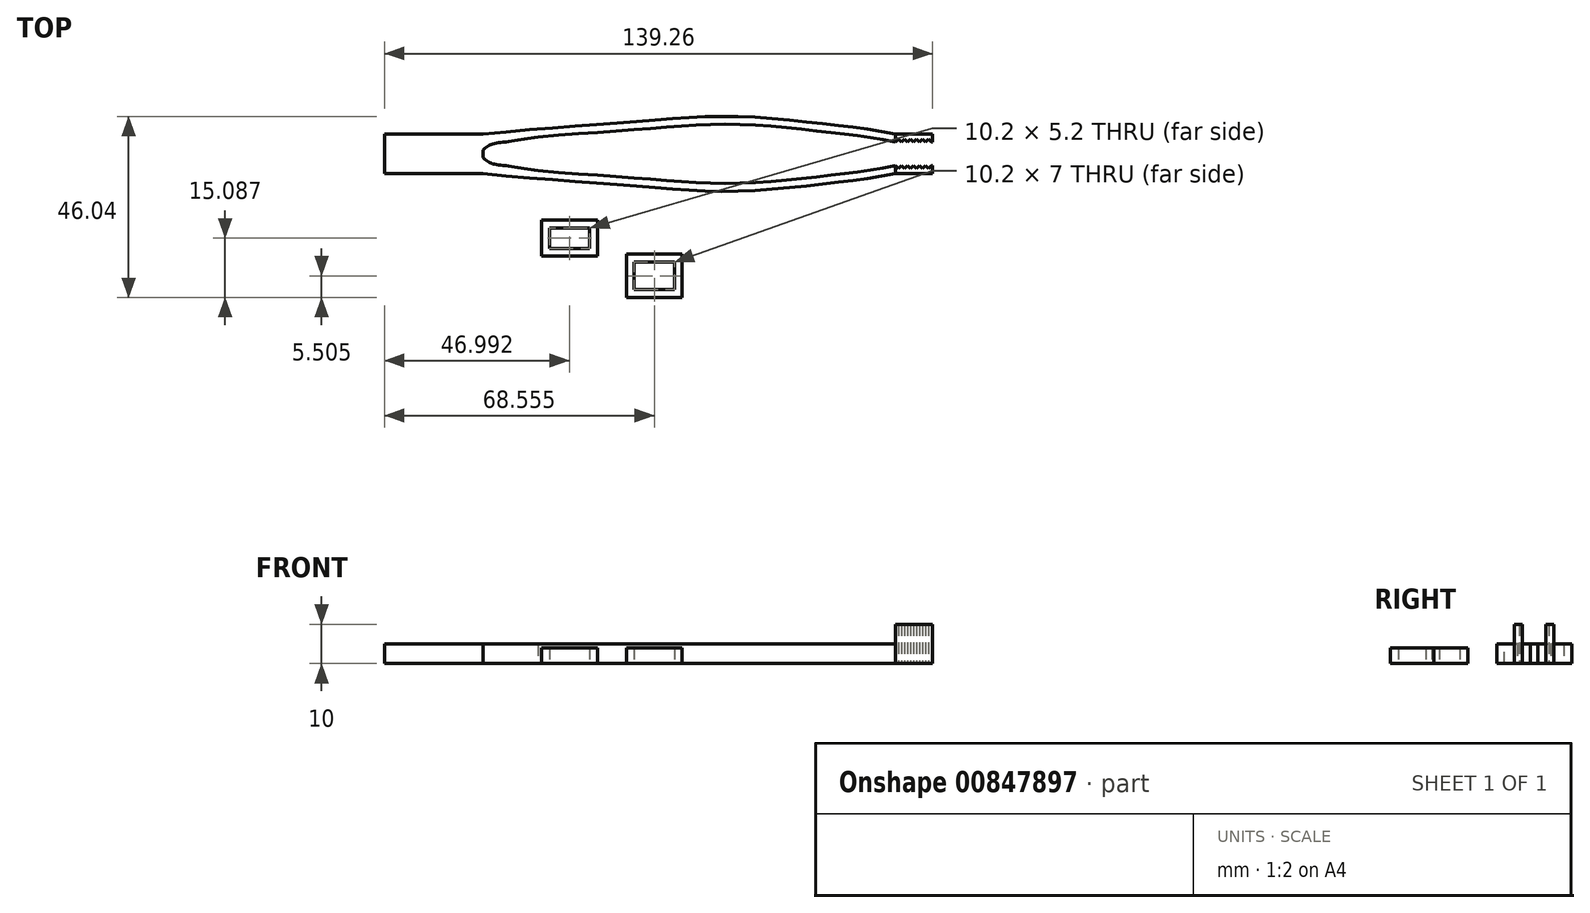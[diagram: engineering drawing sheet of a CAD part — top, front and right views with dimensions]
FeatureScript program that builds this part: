
annotation { "Feature Type Name" : "Feature", "Feature Type Description" : "" }
export const myFeature = defineFeature(function(context is Context, id is Id, definition is map)
    precondition{}
    {
        {
            var Q0;
            Q0=qCreatedBy(makeId("Top.planeOp"),FACE);
            var sketch = newSketch(context, id + "F0", { "sketchPlane" : qUnion([Q0])});
            skLineSegment(sketch, "E0.bottom", {"start": v(-68.5, 5) * mm, "end": v(-93.5, 5) * mm});
            skLineSegment(sketch, "E0.top", {"start": v(-68.5, -5) * mm, "end": v(-93.5, -5) * mm});
            skLineSegment(sketch, "E0.left", {"start": v(-68.5, 0.93) * mm, "end": v(-68.5, -0.93) * mm});
            skLineSegment(sketch, "E0.right", {"start": v(-93.5, 5) * mm, "end": v(-93.5, -5) * mm});
            skPoint(sketch, "E0.middle", {"position": v(-81, 0) * mm});
            skFitSpline(sketch, "E1", {"points": [v(-68.5, 5) * mm, v(-28.51, 8.25) * mm, v(-5, 9.51) * mm, v(18.78, 7.55) * mm, v(36.26, 5) * mm], "startDerivative": vector(137.3, 14.39) * mm, "endDerivative": vector(80, -17.34) * mm});
            skFitSpline(sketch, "E2", {"points": [v(-68.5, 3) * mm, v(-28.51, 6.25) * mm, v(-5, 7.51) * mm, v(18.78, 5.55) * mm, v(36.26, 3) * mm], "startDerivative": vector(137.3, 14.39) * mm, "endDerivative": vector(80, -17.34) * mm});
            skLineSegment(sketch, "E3.bottom", {"start": v(45.46, 3) * mm, "end": v(45.76, 3) * mm});
            skLineSegment(sketch, "E3.top", {"start": v(36.26, 5) * mm, "end": v(45.76, 5) * mm});
            skLineSegment(sketch, "E3.right", {"start": v(45.76, 3) * mm, "end": v(45.76, 5) * mm});
            skFitSpline(sketch, "E4.MirrorCS", {"points": [v(-68.5, -5) * mm, v(-28.51, -8.25) * mm, v(-5, -9.51) * mm, v(18.78, -7.55) * mm, v(36.26, -5) * mm], "startDerivative": vector(137.3, -14.39) * mm, "endDerivative": vector(80, 17.34) * mm});
            skFitSpline(sketch, "E5.MirrorCS", {"points": [v(-68.5, -3) * mm, v(-28.51, -6.25) * mm, v(-5, -7.51) * mm, v(18.78, -5.55) * mm, v(36.26, -3) * mm], "startDerivative": vector(137.3, -14.39) * mm, "endDerivative": vector(80, 17.34) * mm});
            skLineSegment(sketch, "E6.MirrorCS", {"start": v(36.26, -5) * mm, "end": v(45.76, -5) * mm});
            skLineSegment(sketch, "E7.MirrorCS", {"start": v(45.46, -3) * mm, "end": v(45.76, -3) * mm});
            skLineSegment(sketch, "E8.MirrorCS", {"start": v(45.76, -3) * mm, "end": v(45.76, -5) * mm});
            skLineSegment(sketch, "E9", {"start": v(36.26, 3) * mm, "end": v(37.06, 3.77) * mm});
            skLineSegment(sketch, "E10", {"start": v(37.06, 3.77) * mm, "end": v(37.8, 3) * mm});
            skPoint(sketch, "E11.middle", {"position": v(-34.21, 3.16) * mm});
            skLineSegment(sketch, "E12", {"start": v(37.8, 3) * mm, "end": v(38.59, 3.77) * mm});
            skLineSegment(sketch, "E13", {"start": v(38.59, 3.77) * mm, "end": v(39.33, 3) * mm});
            skLineSegment(sketch, "E14", {"start": v(39.33, 3) * mm, "end": v(40.12, 3.77) * mm});
            skLineSegment(sketch, "E15", {"start": v(40.12, 3.77) * mm, "end": v(40.86, 3) * mm});
            skLineSegment(sketch, "E16", {"start": v(40.86, 3) * mm, "end": v(41.65, 3.77) * mm});
            skLineSegment(sketch, "E17", {"start": v(41.65, 3.77) * mm, "end": v(42.4, 3) * mm});
            skLineSegment(sketch, "E18", {"start": v(42.4, 3) * mm, "end": v(43.19, 3.77) * mm});
            skLineSegment(sketch, "E19", {"start": v(43.19, 3.77) * mm, "end": v(43.93, 3) * mm});
            skLineSegment(sketch, "E20", {"start": v(43.93, 3) * mm, "end": v(44.72, 3.77) * mm});
            skLineSegment(sketch, "E21", {"start": v(44.72, 3.77) * mm, "end": v(45.46, 3) * mm});
            skLineSegment(sketch, "E22.MirrorCS", {"start": v(36.26, -3) * mm, "end": v(37.06, -3.77) * mm});
            skLineSegment(sketch, "E23.MirrorCS", {"start": v(37.06, -3.77) * mm, "end": v(37.8, -3) * mm});
            skLineSegment(sketch, "E24.MirrorCS", {"start": v(37.8, -3) * mm, "end": v(38.59, -3.77) * mm});
            skLineSegment(sketch, "E25.MirrorCS", {"start": v(38.59, -3.77) * mm, "end": v(39.33, -3) * mm});
            skLineSegment(sketch, "E26.MirrorCS", {"start": v(39.33, -3) * mm, "end": v(40.12, -3.77) * mm});
            skLineSegment(sketch, "E27.MirrorCS", {"start": v(40.12, -3.77) * mm, "end": v(40.86, -3) * mm});
            skLineSegment(sketch, "E28.MirrorCS", {"start": v(40.86, -3) * mm, "end": v(41.65, -3.77) * mm});
            skLineSegment(sketch, "E29.MirrorCS", {"start": v(41.65, -3.77) * mm, "end": v(42.4, -3) * mm});
            skLineSegment(sketch, "E30.MirrorCS", {"start": v(42.4, -3) * mm, "end": v(43.19, -3.77) * mm});
            skLineSegment(sketch, "E31.MirrorCS", {"start": v(43.19, -3.77) * mm, "end": v(43.93, -3) * mm});
            skLineSegment(sketch, "E32.MirrorCS", {"start": v(43.93, -3) * mm, "end": v(44.72, -3.77) * mm});
            skLineSegment(sketch, "E33.MirrorCS", {"start": v(44.72, -3.77) * mm, "end": v(45.46, -3) * mm});
            skPoint(sketch, "E34.orphan", {"position": v(-46.71, -1.84) * mm});
            skPoint(sketch, "E11.right.start.orphan", {"position": v(-46.71, 8.16) * mm});
            skPoint(sketch, "E35.orphan", {"position": v(-21.71, -1.84) * mm});
            skPoint(sketch, "E11.bottom.start.orphan", {"position": v(-21.71, 8.16) * mm});
            skFitSpline(sketch, "E36", {"points": [v(-68.5, 0.93) * mm, v(-66.67, 2.31) * mm, v(-63.09, 2.98) * mm, v(-54.5, 4.3) * mm], "startDerivative": vector(6.99, 6.69) * mm, "endDerivative": vector(20.32, 3.1) * mm});
            skFitSpline(sketch, "E37.MirrorCS", {"points": [v(-68.5, -0.93) * mm, v(-66.67, -2.31) * mm, v(-63.09, -2.98) * mm, v(-54.5, -4.3) * mm], "startDerivative": vector(6.99, -6.69) * mm, "endDerivative": vector(20.32, -3.1) * mm});
            skSolve(sketch);
        }
        {
            var Q0;
            Q0=makeQuery(id+"F0.imprint","IMPRINT",FACE,{"disambiguationData":[TD([[makeQuery(id+"F0.imprint","IMPRINT",EDGE,{"derivedFrom":sQuery(id+"F0.wireOp",EDGE,"E0.bottom")}),1.0]])]});
            extrude(context, id + "F1", {"entities" : qUnion([Q0]), "depth" : 5 * mm, "offsetDistance" : 25 * mm});
        }
        {
            var Q0;
            Q0=qCreatedBy(makeId("Top.planeOp"),FACE);
            var sketch = newSketch(context, id + "F2", { "sketchPlane" : qUnion([Q0])});
            skLineSegment(sketch, "E38.bottom", {"start": v(-51.6, -24.02) * mm, "end": v(-41.4, -24.02) * mm});
            skLineSegment(sketch, "E38.top", {"start": v(-51.6, -18.82) * mm, "end": v(-41.4, -18.82) * mm});
            skLineSegment(sketch, "E38.left", {"start": v(-51.6, -24.02) * mm, "end": v(-51.6, -18.82) * mm});
            skLineSegment(sketch, "E38.right", {"start": v(-41.4, -24.02) * mm, "end": v(-41.4, -18.82) * mm});
            skLineSegment(sketch, "E39.bottom", {"start": v(-53.6, -26.02) * mm, "end": v(-39.4, -26.02) * mm});
            skLineSegment(sketch, "E39.top", {"start": v(-53.6, -16.82) * mm, "end": v(-39.4, -16.82) * mm});
            skLineSegment(sketch, "E39.left", {"start": v(-53.6, -26.02) * mm, "end": v(-53.6, -16.82) * mm});
            skLineSegment(sketch, "E39.right", {"start": v(-39.4, -26.02) * mm, "end": v(-39.4, -16.82) * mm});
            skLineSegment(sketch, "E40.bottom", {"start": v(-30.04, -34.5) * mm, "end": v(-19.84, -34.5) * mm});
            skLineSegment(sketch, "E40.top", {"start": v(-30.04, -27.5) * mm, "end": v(-19.84, -27.5) * mm});
            skLineSegment(sketch, "E40.left", {"start": v(-30.04, -34.5) * mm, "end": v(-30.04, -27.5) * mm});
            skLineSegment(sketch, "E40.right", {"start": v(-19.84, -34.5) * mm, "end": v(-19.84, -27.5) * mm});
            skLineSegment(sketch, "E41.bottom", {"start": v(-32.04, -36.5) * mm, "end": v(-17.84, -36.5) * mm});
            skLineSegment(sketch, "E41.top", {"start": v(-32.04, -25.5) * mm, "end": v(-17.84, -25.5) * mm});
            skLineSegment(sketch, "E41.left", {"start": v(-32.04, -36.5) * mm, "end": v(-32.04, -25.5) * mm});
            skLineSegment(sketch, "E41.right", {"start": v(-17.84, -36.5) * mm, "end": v(-17.84, -25.5) * mm});
            skSolve(sketch);
        }
        {
            var Q0;
            Q0=makeQuery(id+"F2.imprint","IMPRINT",FACE,{"disambiguationData":[TD([[makeQuery(id+"F2.imprint","IMPRINT",EDGE,{"derivedFrom":sQuery(id+"F2.wireOp",EDGE,"E38.bottom")}),-1.0]])]});
            var Q1;
            Q1=makeQuery(id+"F2.imprint","IMPRINT",FACE,{"disambiguationData":[TD([[makeQuery(id+"F2.imprint","IMPRINT",EDGE,{"derivedFrom":sQuery(id+"F2.wireOp",EDGE,"E40.bottom")}),-1.0]])]});
            extrude(context, id + "F3", {"entities" : qUnion([Q0, Q1]), "depth" : 4 * mm, "offsetDistance" : 25 * mm});
        }
        {
            var Q0;
            Q0=makeQuery(id+"F1.opExtrude","CAP_FACE",FACE,{"disambiguationData":[OSD([sQuery(id+"F0.wireOp",EDGE,"E0.bottom"),sQuery(id+"F0.wireOp",EDGE,"E0.top"),sQuery(id+"F0.wireOp",EDGE,"E0.left"),sQuery(id+"F0.wireOp",EDGE,"E0.right"),sQuery(id+"F0.wireOp",EDGE,"E1"),sQuery(id+"F0.wireOp",EDGE,"E2"),sQuery(id+"F0.wireOp",EDGE,"E3.bottom"),sQuery(id+"F0.wireOp",EDGE,"E3.top"),sQuery(id+"F0.wireOp",EDGE,"E3.right"),sQuery(id+"F0.wireOp",EDGE,"E4.MirrorCS"),sQuery(id+"F0.wireOp",EDGE,"E5.MirrorCS"),sQuery(id+"F0.wireOp",EDGE,"E6.MirrorCS"),sQuery(id+"F0.wireOp",EDGE,"E7.MirrorCS"),sQuery(id+"F0.wireOp",EDGE,"E8.MirrorCS"),sQuery(id+"F0.wireOp",EDGE,"E9"),sQuery(id+"F0.wireOp",EDGE,"E10"),sQuery(id+"F0.wireOp",EDGE,"E12"),sQuery(id+"F0.wireOp",EDGE,"E13"),sQuery(id+"F0.wireOp",EDGE,"E14"),sQuery(id+"F0.wireOp",EDGE,"E15"),sQuery(id+"F0.wireOp",EDGE,"E16"),sQuery(id+"F0.wireOp",EDGE,"E17"),sQuery(id+"F0.wireOp",EDGE,"E18"),sQuery(id+"F0.wireOp",EDGE,"E19"),sQuery(id+"F0.wireOp",EDGE,"E20"),sQuery(id+"F0.wireOp",EDGE,"E21"),sQuery(id+"F0.wireOp",EDGE,"E22.MirrorCS"),sQuery(id+"F0.wireOp",EDGE,"E23.MirrorCS"),sQuery(id+"F0.wireOp",EDGE,"E24.MirrorCS"),sQuery(id+"F0.wireOp",EDGE,"E25.MirrorCS"),sQuery(id+"F0.wireOp",EDGE,"E26.MirrorCS"),sQuery(id+"F0.wireOp",EDGE,"E27.MirrorCS"),sQuery(id+"F0.wireOp",EDGE,"E28.MirrorCS"),sQuery(id+"F0.wireOp",EDGE,"E29.MirrorCS"),sQuery(id+"F0.wireOp",EDGE,"E30.MirrorCS"),sQuery(id+"F0.wireOp",EDGE,"E31.MirrorCS"),sQuery(id+"F0.wireOp",EDGE,"E32.MirrorCS"),sQuery(id+"F0.wireOp",EDGE,"E33.MirrorCS"),sQuery(id+"F0.wireOp",EDGE,"E36"),sQuery(id+"F0.wireOp",EDGE,"E37.MirrorCS")])],"isStart":false});
            var sketch = newSketch(context, id + "F4", { "sketchPlane" : qUnion([Q0])});
            skLineSegment(sketch, "E42", {"start": v(36.26, 3) * mm, "end": v(36.26, 5) * mm});
            skLineSegment(sketch, "E43", {"start": v(36.26, 5) * mm, "end": v(45.76, 5) * mm});
            skLineSegment(sketch, "E44", {"start": v(45.76, 5) * mm, "end": v(45.76, 3) * mm});
            skLineSegment(sketch, "E45", {"start": v(45.76, 3) * mm, "end": v(45.46, 3) * mm});
            skLineSegment(sketch, "E46", {"start": v(45.46, 3) * mm, "end": v(44.72, 3.77) * mm});
            skLineSegment(sketch, "E47", {"start": v(44.72, 3.77) * mm, "end": v(43.93, 3) * mm});
            skLineSegment(sketch, "E48", {"start": v(43.93, 3) * mm, "end": v(43.19, 3.77) * mm});
            skLineSegment(sketch, "E49", {"start": v(43.19, 3.77) * mm, "end": v(42.4, 3) * mm});
            skLineSegment(sketch, "E50", {"start": v(42.4, 3) * mm, "end": v(41.65, 3.77) * mm});
            skLineSegment(sketch, "E51", {"start": v(41.65, 3.77) * mm, "end": v(40.86, 3) * mm});
            skLineSegment(sketch, "E52", {"start": v(40.86, 3) * mm, "end": v(40.12, 3.77) * mm});
            skLineSegment(sketch, "E53", {"start": v(40.12, 3.77) * mm, "end": v(39.33, 3) * mm});
            skLineSegment(sketch, "E54", {"start": v(39.33, 3) * mm, "end": v(38.59, 3.77) * mm});
            skLineSegment(sketch, "E55", {"start": v(38.59, 3.77) * mm, "end": v(37.8, 3) * mm});
            skLineSegment(sketch, "E56", {"start": v(37.8, 3) * mm, "end": v(37.06, 3.77) * mm});
            skLineSegment(sketch, "E57", {"start": v(37.06, 3.77) * mm, "end": v(36.26, 3) * mm});
            skLineSegment(sketch, "E58.MirrorCS", {"start": v(36.26, -3) * mm, "end": v(36.26, -5) * mm});
            skLineSegment(sketch, "E59.MirrorCS", {"start": v(36.26, -5) * mm, "end": v(45.76, -5) * mm});
            skLineSegment(sketch, "E60.MirrorCS", {"start": v(45.76, -5) * mm, "end": v(45.76, -3) * mm});
            skLineSegment(sketch, "E61.MirrorCS", {"start": v(45.76, -3) * mm, "end": v(45.46, -3) * mm});
            skLineSegment(sketch, "E62.MirrorCS", {"start": v(45.46, -3) * mm, "end": v(44.72, -3.77) * mm});
            skLineSegment(sketch, "E63.MirrorCS", {"start": v(44.72, -3.77) * mm, "end": v(43.93, -3) * mm});
            skLineSegment(sketch, "E64.MirrorCS", {"start": v(43.93, -3) * mm, "end": v(43.19, -3.77) * mm});
            skLineSegment(sketch, "E65.MirrorCS", {"start": v(43.19, -3.77) * mm, "end": v(42.4, -3) * mm});
            skLineSegment(sketch, "E66.MirrorCS", {"start": v(42.4, -3) * mm, "end": v(41.65, -3.77) * mm});
            skLineSegment(sketch, "E67.MirrorCS", {"start": v(41.65, -3.77) * mm, "end": v(40.86, -3) * mm});
            skLineSegment(sketch, "E68.MirrorCS", {"start": v(40.86, -3) * mm, "end": v(40.12, -3.77) * mm});
            skLineSegment(sketch, "E69.MirrorCS", {"start": v(40.12, -3.77) * mm, "end": v(39.33, -3) * mm});
            skLineSegment(sketch, "E70.MirrorCS", {"start": v(39.33, -3) * mm, "end": v(38.59, -3.77) * mm});
            skLineSegment(sketch, "E71.MirrorCS", {"start": v(38.59, -3.77) * mm, "end": v(37.8, -3) * mm});
            skLineSegment(sketch, "E72.MirrorCS", {"start": v(37.8, -3) * mm, "end": v(37.06, -3.77) * mm});
            skLineSegment(sketch, "E73.MirrorCS", {"start": v(37.06, -3.77) * mm, "end": v(36.26, -3) * mm});
            skSolve(sketch);
        }
        {
            var Q0;
            Q0=makeQuery(id+"F4.imprint","IMPRINT",FACE,{"disambiguationData":[TD([[makeQuery(id+"F4.imprint","IMPRINT",EDGE,{"derivedFrom":sQuery(id+"F4.wireOp",EDGE,"E42")}),-1.0]])]});
            var Q1;
            Q1=makeQuery(id+"F4.imprint","IMPRINT",FACE,{"disambiguationData":[TD([[makeQuery(id+"F4.imprint","IMPRINT",EDGE,{"derivedFrom":sQuery(id+"F4.wireOp",EDGE,"E58.MirrorCS")}),1.0]])]});
            extrude(context, id + "F5", {"entities" : qUnion([Q0, Q1]), "operationType" : NewBodyOperationType.ADD, "depth" : 5 * mm, "offsetDistance" : 25 * mm});
        }
    });
